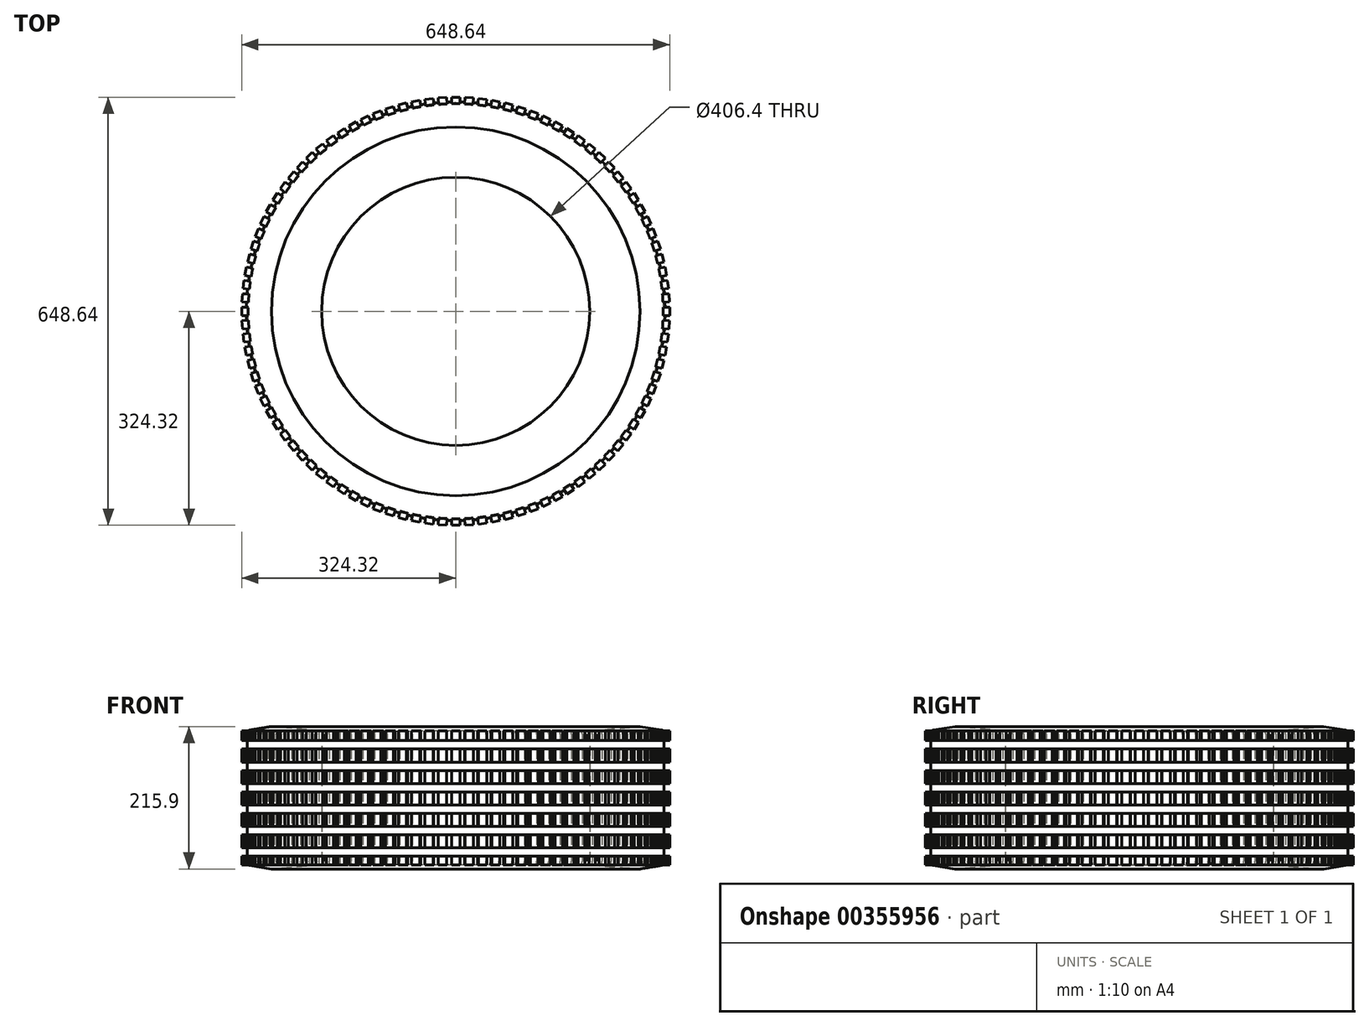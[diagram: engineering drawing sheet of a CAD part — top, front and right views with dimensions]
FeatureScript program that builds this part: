
annotation { "Feature Type Name" : "Feature", "Feature Type Description" : "" }
export const myFeature = defineFeature(function(context is Context, id is Id, definition is map)
    precondition{}
    {
        {
            var Q0;
            Q0=qCreatedBy(makeId("Top.planeOp"),FACE);
            var sketch = newSketch(context, id + "F0", { "sketchPlane" : qUnion([Q0])});
            skCircle(sketch, "E0", {"center": v(0, 0) * mm, "radius": 317.5 * mm});
            skCircle(sketch, "E1", {"center": v(0, 0) * mm, "radius": 203.2 * mm});
            skLineSegment(sketch, "E2", {"start": v(0, 0) * mm, "end": v(0, 317.5) * mm});
            skSolve(sketch);
        }
        {
            var Q0;
            Q0=qSketchRegion(id+"F0",true);
            extrude(context, id + "F1", {"entities" : qUnion([Q0]), "depth" : 209.55 * mm, "hasSecondDirection" : true, "secondDirectionOppositeDirection" : true, "secondDirectionDepth" : 6.35 * mm});
        }
        {
            var Q0;
            Q0=makeQuery(id+"F1.opExtrude","CAP_EDGE",EDGE,{"disambiguationData":[OSD([sQuery(id+"F0.wireOp",EDGE,"E0")])],"isStart":true});
            chamfer(context, id + "F2", {"entities" : qUnion([Q0]), "chamferType" : ChamferType.TWO_OFFSETS, "width1" : 6.35 * mm, "oppositeDirection" : false, "width2" : 38.1 * mm, "tangentPropagation" : true});
        }
        {
            var Q0;
            Q0=makeQuery(id+"F1.opExtrude","CAP_EDGE",EDGE,{"disambiguationData":[OSD([sQuery(id+"F0.wireOp",EDGE,"E0")])],"isStart":false});
            chamfer(context, id + "F3", {"entities" : qUnion([Q0]), "chamferType" : ChamferType.TWO_OFFSETS, "width1" : 6.35 * mm, "oppositeDirection" : true, "width2" : 38.1 * mm, "tangentPropagation" : true});
        }
        {
            var Q0;
            Q0=makeQuery(id+"F1.opExtrude","CAP_EDGE",EDGE,{"disambiguationData":[OSD([sQuery(id+"F0.wireOp",EDGE,"E1")])],"isStart":true});
            chamfer(context, id + "F4", {"entities" : qUnion([Q0]), "chamferType" : ChamferType.TWO_OFFSETS, "width1" : 76.2 * mm, "oppositeDirection" : false, "width2" : 6.35 * mm, "tangentPropagation" : true});
        }
        {
            var Q0;
            Q0=makeQuery(id+"F1.opExtrude","CAP_EDGE",EDGE,{"disambiguationData":[OSD([sQuery(id+"F0.wireOp",EDGE,"E1")])],"isStart":false});
            chamfer(context, id + "F5", {"entities" : qUnion([Q0]), "chamferType" : ChamferType.TWO_OFFSETS, "width1" : 6.35 * mm, "oppositeDirection" : false, "width2" : 76.2 * mm, "tangentPropagation" : true});
        }
        {
            var Q0;
            {var subQ0=sQuery(id+"F0.wireOp",EDGE,"E0");Q0=makeQuery(id+"F2.opChamfer","BLEND_EDGE",EDGE,{"blendedFrom":[makeQuery(id+"F1.opExtrude","CAP_EDGE",EDGE,{"disambiguationData":[OSD([subQ0])],"isStart":true}),makeQuery(id+"F1.opExtrude","SWEPT_FACE",FACE,{"disambiguationData":[OSD([subQ0])]})],"blendedInto":[makeQuery(id+"F1.opExtrude","SWEPT_FACE",FACE,{"disambiguationData":[OSD([subQ0])]})]});}
            var Q1;
            {var subQ0=sQuery(id+"F0.wireOp",EDGE,"E0");Q1=makeQuery(id+"F3.opChamfer","BLEND_EDGE",EDGE,{"blendedFrom":[makeQuery(id+"F1.opExtrude","CAP_EDGE",EDGE,{"disambiguationData":[OSD([subQ0])],"isStart":false}),makeQuery(id+"F1.opExtrude","SWEPT_FACE",FACE,{"disambiguationData":[OSD([subQ0])]})],"blendedInto":[makeQuery(id+"F1.opExtrude","SWEPT_FACE",FACE,{"disambiguationData":[OSD([subQ0])]})]});}
            fillet(context, id + "F6", {"entities" : qUnion([Q0, Q1]), "radius" : 6.35 * mm, "tangentPropagation" : true, "allowEdgeOverflow" : false});
        }
        {
            var Q0;
            Q0=qCreatedBy(makeId("Top.planeOp"),FACE);
            var sketch = newSketch(context, id + "F7", { "sketchPlane" : qUnion([Q0])});
            skLineSegment(sketch, "E3.bottom", {"start": v(6.35, -311.62) * mm, "end": v(-6.35, -311.62) * mm});
            skLineSegment(sketch, "E3.top", {"start": v(6.35, -324.32) * mm, "end": v(-6.35, -324.32) * mm});
            skLineSegment(sketch, "E3.left", {"start": v(6.35, -311.62) * mm, "end": v(6.35, -324.32) * mm});
            skLineSegment(sketch, "E3.right", {"start": v(-6.35, -311.62) * mm, "end": v(-6.35, -324.32) * mm});
            skPoint(sketch, "E3.middle", {"position": v(0, -317.97) * mm});
            skLineSegment(sketch, "E4.1.0", {"start": v(13.23, -311.4) * mm, "end": v(14.03, -324.08) * mm});
            skLineSegment(sketch, "E4.1.1", {"start": v(25.9, -310.61) * mm, "end": v(26.7, -323.29) * mm});
            skLineSegment(sketch, "E4.1.2", {"start": v(26.7, -323.29) * mm, "end": v(14.03, -324.08) * mm});
            skLineSegment(sketch, "E4.1.3", {"start": v(25.9, -310.61) * mm, "end": v(13.23, -311.4) * mm});
            skLineSegment(sketch, "E4.2.0", {"start": v(32.76, -309.96) * mm, "end": v(34.35, -322.56) * mm});
            skLineSegment(sketch, "E4.2.1", {"start": v(45.36, -308.37) * mm, "end": v(46.95, -320.97) * mm});
            skLineSegment(sketch, "E4.2.2", {"start": v(46.95, -320.97) * mm, "end": v(34.35, -322.56) * mm});
            skLineSegment(sketch, "E4.2.3", {"start": v(45.36, -308.37) * mm, "end": v(32.76, -309.96) * mm});
            skLineSegment(sketch, "E4.3.0", {"start": v(52.15, -307.3) * mm, "end": v(54.53, -319.77) * mm});
            skLineSegment(sketch, "E4.3.1", {"start": v(64.63, -304.91) * mm, "end": v(67, -317.39) * mm});
            skLineSegment(sketch, "E4.3.2", {"start": v(67, -317.39) * mm, "end": v(54.53, -319.77) * mm});
            skLineSegment(sketch, "E4.3.3", {"start": v(64.63, -304.91) * mm, "end": v(52.15, -307.3) * mm});
            skLineSegment(sketch, "E4.4.0", {"start": v(71.35, -303.41) * mm, "end": v(74.5, -315.71) * mm});
            skLineSegment(sketch, "E4.4.1", {"start": v(83.65, -300.25) * mm, "end": v(86.8, -312.56) * mm});
            skLineSegment(sketch, "E4.4.2", {"start": v(86.8, -312.56) * mm, "end": v(74.5, -315.71) * mm});
            skLineSegment(sketch, "E4.4.3", {"start": v(83.65, -300.25) * mm, "end": v(71.35, -303.41) * mm});
            skLineSegment(sketch, "E4.5.0", {"start": v(90.26, -298.33) * mm, "end": v(94.18, -310.41) * mm});
            skLineSegment(sketch, "E4.5.1", {"start": v(102.34, -294.4) * mm, "end": v(106.26, -306.49) * mm});
            skLineSegment(sketch, "E4.5.2", {"start": v(106.26, -306.49) * mm, "end": v(94.18, -310.41) * mm});
            skLineSegment(sketch, "E4.5.3", {"start": v(102.34, -294.4) * mm, "end": v(90.26, -298.33) * mm});
            skLineSegment(sketch, "E4.6.0", {"start": v(108.81, -292.08) * mm, "end": v(113.49, -303.89) * mm});
            skLineSegment(sketch, "E4.6.1", {"start": v(120.62, -287.4) * mm, "end": v(125.3, -299.21) * mm});
            skLineSegment(sketch, "E4.6.2", {"start": v(125.3, -299.21) * mm, "end": v(113.49, -303.89) * mm});
            skLineSegment(sketch, "E4.6.3", {"start": v(120.62, -287.4) * mm, "end": v(108.81, -292.08) * mm});
            skLineSegment(sketch, "E4.7.0", {"start": v(126.94, -284.67) * mm, "end": v(132.34, -296.16) * mm});
            skLineSegment(sketch, "E4.7.1", {"start": v(138.43, -279.26) * mm, "end": v(143.84, -290.75) * mm});
            skLineSegment(sketch, "E4.7.2", {"start": v(143.84, -290.75) * mm, "end": v(132.34, -296.16) * mm});
            skLineSegment(sketch, "E4.7.3", {"start": v(138.43, -279.26) * mm, "end": v(126.94, -284.67) * mm});
            skLineSegment(sketch, "E4.8.0", {"start": v(144.56, -276.14) * mm, "end": v(150.68, -287.27) * mm});
            skLineSegment(sketch, "E4.8.1", {"start": v(155.7, -270.02) * mm, "end": v(161.8, -281.15) * mm});
            skLineSegment(sketch, "E4.8.2", {"start": v(161.8, -281.15) * mm, "end": v(150.68, -287.27) * mm});
            skLineSegment(sketch, "E4.8.3", {"start": v(155.7, -270.02) * mm, "end": v(144.56, -276.14) * mm});
            skLineSegment(sketch, "E4.9.0", {"start": v(161.61, -266.52) * mm, "end": v(168.42, -277.24) * mm});
            skLineSegment(sketch, "E4.9.1", {"start": v(172.34, -259.71) * mm, "end": v(179.14, -270.43) * mm});
            skLineSegment(sketch, "E4.9.2", {"start": v(179.14, -270.43) * mm, "end": v(168.42, -277.24) * mm});
            skLineSegment(sketch, "E4.9.3", {"start": v(172.34, -259.71) * mm, "end": v(161.61, -266.52) * mm});
            skLineSegment(sketch, "E4.10.0", {"start": v(178.03, -255.84) * mm, "end": v(185.5, -266.12) * mm});
            skLineSegment(sketch, "E4.10.1", {"start": v(188.3, -248.38) * mm, "end": v(195.77, -258.65) * mm});
            skLineSegment(sketch, "E4.10.2", {"start": v(195.77, -258.65) * mm, "end": v(185.5, -266.12) * mm});
            skLineSegment(sketch, "E4.10.3", {"start": v(188.3, -248.38) * mm, "end": v(178.03, -255.84) * mm});
            skLineSegment(sketch, "E4.11.0", {"start": v(193.74, -244.16) * mm, "end": v(201.84, -253.94) * mm});
            skLineSegment(sketch, "E4.11.1", {"start": v(203.53, -236.06) * mm, "end": v(211.62, -245.85) * mm});
            skLineSegment(sketch, "E4.11.2", {"start": v(211.62, -245.85) * mm, "end": v(201.84, -253.94) * mm});
            skLineSegment(sketch, "E4.11.3", {"start": v(203.53, -236.06) * mm, "end": v(193.74, -244.16) * mm});
            skLineSegment(sketch, "E4.12.0", {"start": v(208.7, -231.51) * mm, "end": v(217.39, -240.77) * mm});
            skLineSegment(sketch, "E4.12.1", {"start": v(217.95, -222.82) * mm, "end": v(226.64, -232.08) * mm});
            skLineSegment(sketch, "E4.12.2", {"start": v(226.64, -232.08) * mm, "end": v(217.39, -240.77) * mm});
            skLineSegment(sketch, "E4.12.3", {"start": v(217.95, -222.82) * mm, "end": v(208.7, -231.51) * mm});
            skLineSegment(sketch, "E4.13.0", {"start": v(222.82, -217.95) * mm, "end": v(232.08, -226.64) * mm});
            skLineSegment(sketch, "E4.13.1", {"start": v(231.51, -208.7) * mm, "end": v(240.77, -217.39) * mm});
            skLineSegment(sketch, "E4.13.2", {"start": v(240.77, -217.39) * mm, "end": v(232.08, -226.64) * mm});
            skLineSegment(sketch, "E4.13.3", {"start": v(231.51, -208.7) * mm, "end": v(222.82, -217.95) * mm});
            skLineSegment(sketch, "E4.14.0", {"start": v(236.06, -203.53) * mm, "end": v(245.85, -211.62) * mm});
            skLineSegment(sketch, "E4.14.1", {"start": v(244.16, -193.74) * mm, "end": v(253.94, -201.84) * mm});
            skLineSegment(sketch, "E4.14.2", {"start": v(253.94, -201.84) * mm, "end": v(245.85, -211.62) * mm});
            skLineSegment(sketch, "E4.14.3", {"start": v(244.16, -193.74) * mm, "end": v(236.06, -203.53) * mm});
            skLineSegment(sketch, "E4.15.0", {"start": v(248.38, -188.3) * mm, "end": v(258.65, -195.77) * mm});
            skLineSegment(sketch, "E4.15.1", {"start": v(255.84, -178.03) * mm, "end": v(266.12, -185.5) * mm});
            skLineSegment(sketch, "E4.15.2", {"start": v(266.12, -185.5) * mm, "end": v(258.65, -195.77) * mm});
            skLineSegment(sketch, "E4.15.3", {"start": v(255.84, -178.03) * mm, "end": v(248.38, -188.3) * mm});
            skLineSegment(sketch, "E4.16.0", {"start": v(259.71, -172.34) * mm, "end": v(270.43, -179.14) * mm});
            skLineSegment(sketch, "E4.16.1", {"start": v(266.52, -161.61) * mm, "end": v(277.24, -168.42) * mm});
            skLineSegment(sketch, "E4.16.2", {"start": v(277.24, -168.42) * mm, "end": v(270.43, -179.14) * mm});
            skLineSegment(sketch, "E4.16.3", {"start": v(266.52, -161.61) * mm, "end": v(259.71, -172.34) * mm});
            skLineSegment(sketch, "E4.17.0", {"start": v(270.02, -155.7) * mm, "end": v(281.15, -161.8) * mm});
            skLineSegment(sketch, "E4.17.1", {"start": v(276.14, -144.56) * mm, "end": v(287.27, -150.68) * mm});
            skLineSegment(sketch, "E4.17.2", {"start": v(287.27, -150.68) * mm, "end": v(281.15, -161.8) * mm});
            skLineSegment(sketch, "E4.17.3", {"start": v(276.14, -144.56) * mm, "end": v(270.02, -155.7) * mm});
            skLineSegment(sketch, "E4.18.0", {"start": v(279.26, -138.43) * mm, "end": v(290.75, -143.84) * mm});
            skLineSegment(sketch, "E4.18.1", {"start": v(284.67, -126.94) * mm, "end": v(296.16, -132.34) * mm});
            skLineSegment(sketch, "E4.18.2", {"start": v(296.16, -132.34) * mm, "end": v(290.75, -143.84) * mm});
            skLineSegment(sketch, "E4.18.3", {"start": v(284.67, -126.94) * mm, "end": v(279.26, -138.43) * mm});
            skLineSegment(sketch, "E4.19.0", {"start": v(287.4, -120.62) * mm, "end": v(299.21, -125.3) * mm});
            skLineSegment(sketch, "E4.19.1", {"start": v(292.08, -108.81) * mm, "end": v(303.89, -113.49) * mm});
            skLineSegment(sketch, "E4.19.2", {"start": v(303.89, -113.49) * mm, "end": v(299.21, -125.3) * mm});
            skLineSegment(sketch, "E4.19.3", {"start": v(292.08, -108.81) * mm, "end": v(287.4, -120.62) * mm});
            skLineSegment(sketch, "E4.20.0", {"start": v(294.4, -102.34) * mm, "end": v(306.49, -106.26) * mm});
            skLineSegment(sketch, "E4.20.1", {"start": v(298.33, -90.26) * mm, "end": v(310.41, -94.18) * mm});
            skLineSegment(sketch, "E4.20.2", {"start": v(310.41, -94.18) * mm, "end": v(306.49, -106.26) * mm});
            skLineSegment(sketch, "E4.20.3", {"start": v(298.33, -90.26) * mm, "end": v(294.4, -102.34) * mm});
            skLineSegment(sketch, "E4.21.0", {"start": v(300.25, -83.65) * mm, "end": v(312.56, -86.8) * mm});
            skLineSegment(sketch, "E4.21.1", {"start": v(303.41, -71.35) * mm, "end": v(315.71, -74.5) * mm});
            skLineSegment(sketch, "E4.21.2", {"start": v(315.71, -74.5) * mm, "end": v(312.56, -86.8) * mm});
            skLineSegment(sketch, "E4.21.3", {"start": v(303.41, -71.35) * mm, "end": v(300.25, -83.65) * mm});
            skLineSegment(sketch, "E4.22.0", {"start": v(304.91, -64.63) * mm, "end": v(317.39, -67) * mm});
            skLineSegment(sketch, "E4.22.1", {"start": v(307.3, -52.15) * mm, "end": v(319.77, -54.53) * mm});
            skLineSegment(sketch, "E4.22.2", {"start": v(319.77, -54.53) * mm, "end": v(317.39, -67) * mm});
            skLineSegment(sketch, "E4.22.3", {"start": v(307.3, -52.15) * mm, "end": v(304.91, -64.63) * mm});
            skLineSegment(sketch, "E4.23.0", {"start": v(308.37, -45.36) * mm, "end": v(320.97, -46.95) * mm});
            skLineSegment(sketch, "E4.23.1", {"start": v(309.96, -32.76) * mm, "end": v(322.56, -34.35) * mm});
            skLineSegment(sketch, "E4.23.2", {"start": v(322.56, -34.35) * mm, "end": v(320.97, -46.95) * mm});
            skLineSegment(sketch, "E4.23.3", {"start": v(309.96, -32.76) * mm, "end": v(308.37, -45.36) * mm});
            skLineSegment(sketch, "E4.24.0", {"start": v(310.61, -25.9) * mm, "end": v(323.29, -26.7) * mm});
            skLineSegment(sketch, "E4.24.1", {"start": v(311.4, -13.23) * mm, "end": v(324.08, -14.03) * mm});
            skLineSegment(sketch, "E4.24.2", {"start": v(324.08, -14.03) * mm, "end": v(323.29, -26.7) * mm});
            skLineSegment(sketch, "E4.24.3", {"start": v(311.4, -13.23) * mm, "end": v(310.61, -25.9) * mm});
            skLineSegment(sketch, "E4.25.0", {"start": v(311.62, -6.35) * mm, "end": v(324.32, -6.35) * mm});
            skLineSegment(sketch, "E4.25.1", {"start": v(311.62, 6.35) * mm, "end": v(324.32, 6.35) * mm});
            skLineSegment(sketch, "E4.25.2", {"start": v(324.32, 6.35) * mm, "end": v(324.32, -6.35) * mm});
            skLineSegment(sketch, "E4.25.3", {"start": v(311.62, 6.35) * mm, "end": v(311.62, -6.35) * mm});
            skLineSegment(sketch, "E4.26.0", {"start": v(311.4, 13.23) * mm, "end": v(324.08, 14.03) * mm});
            skLineSegment(sketch, "E4.26.1", {"start": v(310.61, 25.9) * mm, "end": v(323.29, 26.7) * mm});
            skLineSegment(sketch, "E4.26.2", {"start": v(323.29, 26.7) * mm, "end": v(324.08, 14.03) * mm});
            skLineSegment(sketch, "E4.26.3", {"start": v(310.61, 25.9) * mm, "end": v(311.4, 13.23) * mm});
            skLineSegment(sketch, "E4.27.0", {"start": v(309.96, 32.76) * mm, "end": v(322.56, 34.35) * mm});
            skLineSegment(sketch, "E4.27.1", {"start": v(308.37, 45.36) * mm, "end": v(320.97, 46.95) * mm});
            skLineSegment(sketch, "E4.27.2", {"start": v(320.97, 46.95) * mm, "end": v(322.56, 34.35) * mm});
            skLineSegment(sketch, "E4.27.3", {"start": v(308.37, 45.36) * mm, "end": v(309.96, 32.76) * mm});
            skLineSegment(sketch, "E4.28.0", {"start": v(307.3, 52.15) * mm, "end": v(319.77, 54.53) * mm});
            skLineSegment(sketch, "E4.28.1", {"start": v(304.91, 64.63) * mm, "end": v(317.39, 67) * mm});
            skLineSegment(sketch, "E4.28.2", {"start": v(317.39, 67) * mm, "end": v(319.77, 54.53) * mm});
            skLineSegment(sketch, "E4.28.3", {"start": v(304.91, 64.63) * mm, "end": v(307.3, 52.15) * mm});
            skLineSegment(sketch, "E4.29.0", {"start": v(303.41, 71.35) * mm, "end": v(315.71, 74.5) * mm});
            skLineSegment(sketch, "E4.29.1", {"start": v(300.25, 83.65) * mm, "end": v(312.56, 86.8) * mm});
            skLineSegment(sketch, "E4.29.2", {"start": v(312.56, 86.8) * mm, "end": v(315.71, 74.5) * mm});
            skLineSegment(sketch, "E4.29.3", {"start": v(300.25, 83.65) * mm, "end": v(303.41, 71.35) * mm});
            skLineSegment(sketch, "E4.30.0", {"start": v(298.33, 90.26) * mm, "end": v(310.41, 94.18) * mm});
            skLineSegment(sketch, "E4.30.1", {"start": v(294.4, 102.34) * mm, "end": v(306.49, 106.26) * mm});
            skLineSegment(sketch, "E4.30.2", {"start": v(306.49, 106.26) * mm, "end": v(310.41, 94.18) * mm});
            skLineSegment(sketch, "E4.30.3", {"start": v(294.4, 102.34) * mm, "end": v(298.33, 90.26) * mm});
            skLineSegment(sketch, "E4.31.0", {"start": v(292.08, 108.81) * mm, "end": v(303.89, 113.49) * mm});
            skLineSegment(sketch, "E4.31.1", {"start": v(287.4, 120.62) * mm, "end": v(299.21, 125.3) * mm});
            skLineSegment(sketch, "E4.31.2", {"start": v(299.21, 125.3) * mm, "end": v(303.89, 113.49) * mm});
            skLineSegment(sketch, "E4.31.3", {"start": v(287.4, 120.62) * mm, "end": v(292.08, 108.81) * mm});
            skLineSegment(sketch, "E4.32.0", {"start": v(284.67, 126.94) * mm, "end": v(296.16, 132.34) * mm});
            skLineSegment(sketch, "E4.32.1", {"start": v(279.26, 138.43) * mm, "end": v(290.75, 143.84) * mm});
            skLineSegment(sketch, "E4.32.2", {"start": v(290.75, 143.84) * mm, "end": v(296.16, 132.34) * mm});
            skLineSegment(sketch, "E4.32.3", {"start": v(279.26, 138.43) * mm, "end": v(284.67, 126.94) * mm});
            skLineSegment(sketch, "E4.33.0", {"start": v(276.14, 144.56) * mm, "end": v(287.27, 150.68) * mm});
            skLineSegment(sketch, "E4.33.1", {"start": v(270.02, 155.7) * mm, "end": v(281.15, 161.8) * mm});
            skLineSegment(sketch, "E4.33.2", {"start": v(281.15, 161.8) * mm, "end": v(287.27, 150.68) * mm});
            skLineSegment(sketch, "E4.33.3", {"start": v(270.02, 155.7) * mm, "end": v(276.14, 144.56) * mm});
            skLineSegment(sketch, "E4.34.0", {"start": v(266.52, 161.61) * mm, "end": v(277.24, 168.42) * mm});
            skLineSegment(sketch, "E4.34.1", {"start": v(259.71, 172.34) * mm, "end": v(270.43, 179.14) * mm});
            skLineSegment(sketch, "E4.34.2", {"start": v(270.43, 179.14) * mm, "end": v(277.24, 168.42) * mm});
            skLineSegment(sketch, "E4.34.3", {"start": v(259.71, 172.34) * mm, "end": v(266.52, 161.61) * mm});
            skLineSegment(sketch, "E4.35.0", {"start": v(255.84, 178.03) * mm, "end": v(266.12, 185.5) * mm});
            skLineSegment(sketch, "E4.35.1", {"start": v(248.38, 188.3) * mm, "end": v(258.65, 195.77) * mm});
            skLineSegment(sketch, "E4.35.2", {"start": v(258.65, 195.77) * mm, "end": v(266.12, 185.5) * mm});
            skLineSegment(sketch, "E4.35.3", {"start": v(248.38, 188.3) * mm, "end": v(255.84, 178.03) * mm});
            skLineSegment(sketch, "E4.36.0", {"start": v(244.16, 193.74) * mm, "end": v(253.94, 201.84) * mm});
            skLineSegment(sketch, "E4.36.1", {"start": v(236.06, 203.53) * mm, "end": v(245.85, 211.62) * mm});
            skLineSegment(sketch, "E4.36.2", {"start": v(245.85, 211.62) * mm, "end": v(253.94, 201.84) * mm});
            skLineSegment(sketch, "E4.36.3", {"start": v(236.06, 203.53) * mm, "end": v(244.16, 193.74) * mm});
            skLineSegment(sketch, "E4.37.0", {"start": v(231.51, 208.7) * mm, "end": v(240.77, 217.39) * mm});
            skLineSegment(sketch, "E4.37.1", {"start": v(222.82, 217.95) * mm, "end": v(232.08, 226.64) * mm});
            skLineSegment(sketch, "E4.37.2", {"start": v(232.08, 226.64) * mm, "end": v(240.77, 217.39) * mm});
            skLineSegment(sketch, "E4.37.3", {"start": v(222.82, 217.95) * mm, "end": v(231.51, 208.7) * mm});
            skLineSegment(sketch, "E4.38.0", {"start": v(217.95, 222.82) * mm, "end": v(226.64, 232.08) * mm});
            skLineSegment(sketch, "E4.38.1", {"start": v(208.7, 231.51) * mm, "end": v(217.39, 240.77) * mm});
            skLineSegment(sketch, "E4.38.2", {"start": v(217.39, 240.77) * mm, "end": v(226.64, 232.08) * mm});
            skLineSegment(sketch, "E4.38.3", {"start": v(208.7, 231.51) * mm, "end": v(217.95, 222.82) * mm});
            skLineSegment(sketch, "E4.39.0", {"start": v(203.53, 236.06) * mm, "end": v(211.62, 245.85) * mm});
            skLineSegment(sketch, "E4.39.1", {"start": v(193.74, 244.16) * mm, "end": v(201.84, 253.94) * mm});
            skLineSegment(sketch, "E4.39.2", {"start": v(201.84, 253.94) * mm, "end": v(211.62, 245.85) * mm});
            skLineSegment(sketch, "E4.39.3", {"start": v(193.74, 244.16) * mm, "end": v(203.53, 236.06) * mm});
            skLineSegment(sketch, "E4.40.0", {"start": v(188.3, 248.38) * mm, "end": v(195.77, 258.65) * mm});
            skLineSegment(sketch, "E4.40.1", {"start": v(178.03, 255.84) * mm, "end": v(185.5, 266.12) * mm});
            skLineSegment(sketch, "E4.40.2", {"start": v(185.5, 266.12) * mm, "end": v(195.77, 258.65) * mm});
            skLineSegment(sketch, "E4.40.3", {"start": v(178.03, 255.84) * mm, "end": v(188.3, 248.38) * mm});
            skLineSegment(sketch, "E4.41.0", {"start": v(172.34, 259.71) * mm, "end": v(179.14, 270.43) * mm});
            skLineSegment(sketch, "E4.41.1", {"start": v(161.61, 266.52) * mm, "end": v(168.42, 277.24) * mm});
            skLineSegment(sketch, "E4.41.2", {"start": v(168.42, 277.24) * mm, "end": v(179.14, 270.43) * mm});
            skLineSegment(sketch, "E4.41.3", {"start": v(161.61, 266.52) * mm, "end": v(172.34, 259.71) * mm});
            skLineSegment(sketch, "E4.42.0", {"start": v(155.7, 270.02) * mm, "end": v(161.8, 281.15) * mm});
            skLineSegment(sketch, "E4.42.1", {"start": v(144.56, 276.14) * mm, "end": v(150.68, 287.27) * mm});
            skLineSegment(sketch, "E4.42.2", {"start": v(150.68, 287.27) * mm, "end": v(161.8, 281.15) * mm});
            skLineSegment(sketch, "E4.42.3", {"start": v(144.56, 276.14) * mm, "end": v(155.7, 270.02) * mm});
            skLineSegment(sketch, "E4.43.0", {"start": v(138.43, 279.26) * mm, "end": v(143.84, 290.75) * mm});
            skLineSegment(sketch, "E4.43.1", {"start": v(126.94, 284.67) * mm, "end": v(132.34, 296.16) * mm});
            skLineSegment(sketch, "E4.43.2", {"start": v(132.34, 296.16) * mm, "end": v(143.84, 290.75) * mm});
            skLineSegment(sketch, "E4.43.3", {"start": v(126.94, 284.67) * mm, "end": v(138.43, 279.26) * mm});
            skLineSegment(sketch, "E4.44.0", {"start": v(120.62, 287.4) * mm, "end": v(125.3, 299.21) * mm});
            skLineSegment(sketch, "E4.44.1", {"start": v(108.81, 292.08) * mm, "end": v(113.49, 303.89) * mm});
            skLineSegment(sketch, "E4.44.2", {"start": v(113.49, 303.89) * mm, "end": v(125.3, 299.21) * mm});
            skLineSegment(sketch, "E4.44.3", {"start": v(108.81, 292.08) * mm, "end": v(120.62, 287.4) * mm});
            skLineSegment(sketch, "E4.45.0", {"start": v(102.34, 294.4) * mm, "end": v(106.26, 306.49) * mm});
            skLineSegment(sketch, "E4.45.1", {"start": v(90.26, 298.33) * mm, "end": v(94.18, 310.41) * mm});
            skLineSegment(sketch, "E4.45.2", {"start": v(94.18, 310.41) * mm, "end": v(106.26, 306.49) * mm});
            skLineSegment(sketch, "E4.45.3", {"start": v(90.26, 298.33) * mm, "end": v(102.34, 294.4) * mm});
            skLineSegment(sketch, "E4.46.0", {"start": v(83.65, 300.25) * mm, "end": v(86.8, 312.56) * mm});
            skLineSegment(sketch, "E4.46.1", {"start": v(71.35, 303.41) * mm, "end": v(74.5, 315.71) * mm});
            skLineSegment(sketch, "E4.46.2", {"start": v(74.5, 315.71) * mm, "end": v(86.8, 312.56) * mm});
            skLineSegment(sketch, "E4.46.3", {"start": v(71.35, 303.41) * mm, "end": v(83.65, 300.25) * mm});
            skLineSegment(sketch, "E4.47.0", {"start": v(64.63, 304.91) * mm, "end": v(67, 317.39) * mm});
            skLineSegment(sketch, "E4.47.1", {"start": v(52.15, 307.3) * mm, "end": v(54.53, 319.77) * mm});
            skLineSegment(sketch, "E4.47.2", {"start": v(54.53, 319.77) * mm, "end": v(67, 317.39) * mm});
            skLineSegment(sketch, "E4.47.3", {"start": v(52.15, 307.3) * mm, "end": v(64.63, 304.91) * mm});
            skLineSegment(sketch, "E4.48.0", {"start": v(45.36, 308.37) * mm, "end": v(46.95, 320.97) * mm});
            skLineSegment(sketch, "E4.48.1", {"start": v(32.76, 309.96) * mm, "end": v(34.35, 322.56) * mm});
            skLineSegment(sketch, "E4.48.2", {"start": v(34.35, 322.56) * mm, "end": v(46.95, 320.97) * mm});
            skLineSegment(sketch, "E4.48.3", {"start": v(32.76, 309.96) * mm, "end": v(45.36, 308.37) * mm});
            skLineSegment(sketch, "E4.49.0", {"start": v(25.9, 310.61) * mm, "end": v(26.7, 323.29) * mm});
            skLineSegment(sketch, "E4.49.1", {"start": v(13.23, 311.4) * mm, "end": v(14.03, 324.08) * mm});
            skLineSegment(sketch, "E4.49.2", {"start": v(14.03, 324.08) * mm, "end": v(26.7, 323.29) * mm});
            skLineSegment(sketch, "E4.49.3", {"start": v(13.23, 311.4) * mm, "end": v(25.9, 310.61) * mm});
            skLineSegment(sketch, "E4.50.0", {"start": v(6.35, 311.62) * mm, "end": v(6.35, 324.32) * mm});
            skLineSegment(sketch, "E4.50.1", {"start": v(-6.35, 311.62) * mm, "end": v(-6.35, 324.32) * mm});
            skLineSegment(sketch, "E4.50.2", {"start": v(-6.35, 324.32) * mm, "end": v(6.35, 324.32) * mm});
            skLineSegment(sketch, "E4.50.3", {"start": v(-6.35, 311.62) * mm, "end": v(6.35, 311.62) * mm});
            skLineSegment(sketch, "E4.51.0", {"start": v(-13.23, 311.4) * mm, "end": v(-14.03, 324.08) * mm});
            skLineSegment(sketch, "E4.51.1", {"start": v(-25.9, 310.61) * mm, "end": v(-26.7, 323.29) * mm});
            skLineSegment(sketch, "E4.51.2", {"start": v(-26.7, 323.29) * mm, "end": v(-14.03, 324.08) * mm});
            skLineSegment(sketch, "E4.51.3", {"start": v(-25.9, 310.61) * mm, "end": v(-13.23, 311.4) * mm});
            skLineSegment(sketch, "E4.52.0", {"start": v(-32.76, 309.96) * mm, "end": v(-34.35, 322.56) * mm});
            skLineSegment(sketch, "E4.52.1", {"start": v(-45.36, 308.37) * mm, "end": v(-46.95, 320.97) * mm});
            skLineSegment(sketch, "E4.52.2", {"start": v(-46.95, 320.97) * mm, "end": v(-34.35, 322.56) * mm});
            skLineSegment(sketch, "E4.52.3", {"start": v(-45.36, 308.37) * mm, "end": v(-32.76, 309.96) * mm});
            skLineSegment(sketch, "E4.53.0", {"start": v(-52.15, 307.3) * mm, "end": v(-54.53, 319.77) * mm});
            skLineSegment(sketch, "E4.53.1", {"start": v(-64.63, 304.91) * mm, "end": v(-67, 317.39) * mm});
            skLineSegment(sketch, "E4.53.2", {"start": v(-67, 317.39) * mm, "end": v(-54.53, 319.77) * mm});
            skLineSegment(sketch, "E4.53.3", {"start": v(-64.63, 304.91) * mm, "end": v(-52.15, 307.3) * mm});
            skLineSegment(sketch, "E4.54.0", {"start": v(-71.35, 303.41) * mm, "end": v(-74.5, 315.71) * mm});
            skLineSegment(sketch, "E4.54.1", {"start": v(-83.65, 300.25) * mm, "end": v(-86.8, 312.56) * mm});
            skLineSegment(sketch, "E4.54.2", {"start": v(-86.8, 312.56) * mm, "end": v(-74.5, 315.71) * mm});
            skLineSegment(sketch, "E4.54.3", {"start": v(-83.65, 300.25) * mm, "end": v(-71.35, 303.41) * mm});
            skLineSegment(sketch, "E4.55.0", {"start": v(-90.26, 298.33) * mm, "end": v(-94.18, 310.41) * mm});
            skLineSegment(sketch, "E4.55.1", {"start": v(-102.34, 294.4) * mm, "end": v(-106.26, 306.49) * mm});
            skLineSegment(sketch, "E4.55.2", {"start": v(-106.26, 306.49) * mm, "end": v(-94.18, 310.41) * mm});
            skLineSegment(sketch, "E4.55.3", {"start": v(-102.34, 294.4) * mm, "end": v(-90.26, 298.33) * mm});
            skLineSegment(sketch, "E4.56.0", {"start": v(-108.81, 292.08) * mm, "end": v(-113.49, 303.89) * mm});
            skLineSegment(sketch, "E4.56.1", {"start": v(-120.62, 287.4) * mm, "end": v(-125.3, 299.21) * mm});
            skLineSegment(sketch, "E4.56.2", {"start": v(-125.3, 299.21) * mm, "end": v(-113.49, 303.89) * mm});
            skLineSegment(sketch, "E4.56.3", {"start": v(-120.62, 287.4) * mm, "end": v(-108.81, 292.08) * mm});
            skLineSegment(sketch, "E4.57.0", {"start": v(-126.94, 284.67) * mm, "end": v(-132.34, 296.16) * mm});
            skLineSegment(sketch, "E4.57.1", {"start": v(-138.43, 279.26) * mm, "end": v(-143.84, 290.75) * mm});
            skLineSegment(sketch, "E4.57.2", {"start": v(-143.84, 290.75) * mm, "end": v(-132.34, 296.16) * mm});
            skLineSegment(sketch, "E4.57.3", {"start": v(-138.43, 279.26) * mm, "end": v(-126.94, 284.67) * mm});
            skLineSegment(sketch, "E4.58.0", {"start": v(-144.56, 276.14) * mm, "end": v(-150.68, 287.27) * mm});
            skLineSegment(sketch, "E4.58.1", {"start": v(-155.7, 270.02) * mm, "end": v(-161.8, 281.15) * mm});
            skLineSegment(sketch, "E4.58.2", {"start": v(-161.8, 281.15) * mm, "end": v(-150.68, 287.27) * mm});
            skLineSegment(sketch, "E4.58.3", {"start": v(-155.7, 270.02) * mm, "end": v(-144.56, 276.14) * mm});
            skLineSegment(sketch, "E4.59.0", {"start": v(-161.61, 266.52) * mm, "end": v(-168.42, 277.24) * mm});
            skLineSegment(sketch, "E4.59.1", {"start": v(-172.34, 259.71) * mm, "end": v(-179.14, 270.43) * mm});
            skLineSegment(sketch, "E4.59.2", {"start": v(-179.14, 270.43) * mm, "end": v(-168.42, 277.24) * mm});
            skLineSegment(sketch, "E4.59.3", {"start": v(-172.34, 259.71) * mm, "end": v(-161.61, 266.52) * mm});
            skLineSegment(sketch, "E4.60.0", {"start": v(-178.03, 255.84) * mm, "end": v(-185.5, 266.12) * mm});
            skLineSegment(sketch, "E4.60.1", {"start": v(-188.3, 248.38) * mm, "end": v(-195.77, 258.65) * mm});
            skLineSegment(sketch, "E4.60.2", {"start": v(-195.77, 258.65) * mm, "end": v(-185.5, 266.12) * mm});
            skLineSegment(sketch, "E4.60.3", {"start": v(-188.3, 248.38) * mm, "end": v(-178.03, 255.84) * mm});
            skLineSegment(sketch, "E4.61.0", {"start": v(-193.74, 244.16) * mm, "end": v(-201.84, 253.94) * mm});
            skLineSegment(sketch, "E4.61.1", {"start": v(-203.53, 236.06) * mm, "end": v(-211.62, 245.85) * mm});
            skLineSegment(sketch, "E4.61.2", {"start": v(-211.62, 245.85) * mm, "end": v(-201.84, 253.94) * mm});
            skLineSegment(sketch, "E4.61.3", {"start": v(-203.53, 236.06) * mm, "end": v(-193.74, 244.16) * mm});
            skLineSegment(sketch, "E4.62.0", {"start": v(-208.7, 231.51) * mm, "end": v(-217.39, 240.77) * mm});
            skLineSegment(sketch, "E4.62.1", {"start": v(-217.95, 222.82) * mm, "end": v(-226.64, 232.08) * mm});
            skLineSegment(sketch, "E4.62.2", {"start": v(-226.64, 232.08) * mm, "end": v(-217.39, 240.77) * mm});
            skLineSegment(sketch, "E4.62.3", {"start": v(-217.95, 222.82) * mm, "end": v(-208.7, 231.51) * mm});
            skLineSegment(sketch, "E4.63.0", {"start": v(-222.82, 217.95) * mm, "end": v(-232.08, 226.64) * mm});
            skLineSegment(sketch, "E4.63.1", {"start": v(-231.51, 208.7) * mm, "end": v(-240.77, 217.39) * mm});
            skLineSegment(sketch, "E4.63.2", {"start": v(-240.77, 217.39) * mm, "end": v(-232.08, 226.64) * mm});
            skLineSegment(sketch, "E4.63.3", {"start": v(-231.51, 208.7) * mm, "end": v(-222.82, 217.95) * mm});
            skLineSegment(sketch, "E4.64.0", {"start": v(-236.06, 203.53) * mm, "end": v(-245.85, 211.62) * mm});
            skLineSegment(sketch, "E4.64.1", {"start": v(-244.16, 193.74) * mm, "end": v(-253.94, 201.84) * mm});
            skLineSegment(sketch, "E4.64.2", {"start": v(-253.94, 201.84) * mm, "end": v(-245.85, 211.62) * mm});
            skLineSegment(sketch, "E4.64.3", {"start": v(-244.16, 193.74) * mm, "end": v(-236.06, 203.53) * mm});
            skLineSegment(sketch, "E4.65.0", {"start": v(-248.38, 188.3) * mm, "end": v(-258.65, 195.77) * mm});
            skLineSegment(sketch, "E4.65.1", {"start": v(-255.84, 178.03) * mm, "end": v(-266.12, 185.5) * mm});
            skLineSegment(sketch, "E4.65.2", {"start": v(-266.12, 185.5) * mm, "end": v(-258.65, 195.77) * mm});
            skLineSegment(sketch, "E4.65.3", {"start": v(-255.84, 178.03) * mm, "end": v(-248.38, 188.3) * mm});
            skLineSegment(sketch, "E4.66.0", {"start": v(-259.71, 172.34) * mm, "end": v(-270.43, 179.14) * mm});
            skLineSegment(sketch, "E4.66.1", {"start": v(-266.52, 161.61) * mm, "end": v(-277.24, 168.42) * mm});
            skLineSegment(sketch, "E4.66.2", {"start": v(-277.24, 168.42) * mm, "end": v(-270.43, 179.14) * mm});
            skLineSegment(sketch, "E4.66.3", {"start": v(-266.52, 161.61) * mm, "end": v(-259.71, 172.34) * mm});
            skLineSegment(sketch, "E4.67.0", {"start": v(-270.02, 155.7) * mm, "end": v(-281.15, 161.8) * mm});
            skLineSegment(sketch, "E4.67.1", {"start": v(-276.14, 144.56) * mm, "end": v(-287.27, 150.68) * mm});
            skLineSegment(sketch, "E4.67.2", {"start": v(-287.27, 150.68) * mm, "end": v(-281.15, 161.8) * mm});
            skLineSegment(sketch, "E4.67.3", {"start": v(-276.14, 144.56) * mm, "end": v(-270.02, 155.7) * mm});
            skLineSegment(sketch, "E4.68.0", {"start": v(-279.26, 138.43) * mm, "end": v(-290.75, 143.84) * mm});
            skLineSegment(sketch, "E4.68.1", {"start": v(-284.67, 126.94) * mm, "end": v(-296.16, 132.34) * mm});
            skLineSegment(sketch, "E4.68.2", {"start": v(-296.16, 132.34) * mm, "end": v(-290.75, 143.84) * mm});
            skLineSegment(sketch, "E4.68.3", {"start": v(-284.67, 126.94) * mm, "end": v(-279.26, 138.43) * mm});
            skLineSegment(sketch, "E4.69.0", {"start": v(-287.4, 120.62) * mm, "end": v(-299.21, 125.3) * mm});
            skLineSegment(sketch, "E4.69.1", {"start": v(-292.08, 108.81) * mm, "end": v(-303.89, 113.49) * mm});
            skLineSegment(sketch, "E4.69.2", {"start": v(-303.89, 113.49) * mm, "end": v(-299.21, 125.3) * mm});
            skLineSegment(sketch, "E4.69.3", {"start": v(-292.08, 108.81) * mm, "end": v(-287.4, 120.62) * mm});
            skLineSegment(sketch, "E4.70.0", {"start": v(-294.4, 102.34) * mm, "end": v(-306.49, 106.26) * mm});
            skLineSegment(sketch, "E4.70.1", {"start": v(-298.33, 90.26) * mm, "end": v(-310.41, 94.18) * mm});
            skLineSegment(sketch, "E4.70.2", {"start": v(-310.41, 94.18) * mm, "end": v(-306.49, 106.26) * mm});
            skLineSegment(sketch, "E4.70.3", {"start": v(-298.33, 90.26) * mm, "end": v(-294.4, 102.34) * mm});
            skLineSegment(sketch, "E4.71.0", {"start": v(-300.25, 83.65) * mm, "end": v(-312.56, 86.8) * mm});
            skLineSegment(sketch, "E4.71.1", {"start": v(-303.41, 71.35) * mm, "end": v(-315.71, 74.5) * mm});
            skLineSegment(sketch, "E4.71.2", {"start": v(-315.71, 74.5) * mm, "end": v(-312.56, 86.8) * mm});
            skLineSegment(sketch, "E4.71.3", {"start": v(-303.41, 71.35) * mm, "end": v(-300.25, 83.65) * mm});
            skLineSegment(sketch, "E4.72.0", {"start": v(-304.91, 64.63) * mm, "end": v(-317.39, 67) * mm});
            skLineSegment(sketch, "E4.72.1", {"start": v(-307.3, 52.15) * mm, "end": v(-319.77, 54.53) * mm});
            skLineSegment(sketch, "E4.72.2", {"start": v(-319.77, 54.53) * mm, "end": v(-317.39, 67) * mm});
            skLineSegment(sketch, "E4.72.3", {"start": v(-307.3, 52.15) * mm, "end": v(-304.91, 64.63) * mm});
            skLineSegment(sketch, "E4.73.0", {"start": v(-308.37, 45.36) * mm, "end": v(-320.97, 46.95) * mm});
            skLineSegment(sketch, "E4.73.1", {"start": v(-309.96, 32.76) * mm, "end": v(-322.56, 34.35) * mm});
            skLineSegment(sketch, "E4.73.2", {"start": v(-322.56, 34.35) * mm, "end": v(-320.97, 46.95) * mm});
            skLineSegment(sketch, "E4.73.3", {"start": v(-309.96, 32.76) * mm, "end": v(-308.37, 45.36) * mm});
            skLineSegment(sketch, "E4.74.0", {"start": v(-310.61, 25.9) * mm, "end": v(-323.29, 26.7) * mm});
            skLineSegment(sketch, "E4.74.1", {"start": v(-311.4, 13.23) * mm, "end": v(-324.08, 14.03) * mm});
            skLineSegment(sketch, "E4.74.2", {"start": v(-324.08, 14.03) * mm, "end": v(-323.29, 26.7) * mm});
            skLineSegment(sketch, "E4.74.3", {"start": v(-311.4, 13.23) * mm, "end": v(-310.61, 25.9) * mm});
            skLineSegment(sketch, "E4.75.0", {"start": v(-311.62, 6.35) * mm, "end": v(-324.32, 6.35) * mm});
            skLineSegment(sketch, "E4.75.1", {"start": v(-311.62, -6.35) * mm, "end": v(-324.32, -6.35) * mm});
            skLineSegment(sketch, "E4.75.2", {"start": v(-324.32, -6.35) * mm, "end": v(-324.32, 6.35) * mm});
            skLineSegment(sketch, "E4.75.3", {"start": v(-311.62, -6.35) * mm, "end": v(-311.62, 6.35) * mm});
            skLineSegment(sketch, "E4.76.0", {"start": v(-311.4, -13.23) * mm, "end": v(-324.08, -14.03) * mm});
            skLineSegment(sketch, "E4.76.1", {"start": v(-310.61, -25.9) * mm, "end": v(-323.29, -26.7) * mm});
            skLineSegment(sketch, "E4.76.2", {"start": v(-323.29, -26.7) * mm, "end": v(-324.08, -14.03) * mm});
            skLineSegment(sketch, "E4.76.3", {"start": v(-310.61, -25.9) * mm, "end": v(-311.4, -13.23) * mm});
            skLineSegment(sketch, "E4.77.0", {"start": v(-309.96, -32.76) * mm, "end": v(-322.56, -34.35) * mm});
            skLineSegment(sketch, "E4.77.1", {"start": v(-308.37, -45.36) * mm, "end": v(-320.97, -46.95) * mm});
            skLineSegment(sketch, "E4.77.2", {"start": v(-320.97, -46.95) * mm, "end": v(-322.56, -34.35) * mm});
            skLineSegment(sketch, "E4.77.3", {"start": v(-308.37, -45.36) * mm, "end": v(-309.96, -32.76) * mm});
            skLineSegment(sketch, "E4.78.0", {"start": v(-307.3, -52.15) * mm, "end": v(-319.77, -54.53) * mm});
            skLineSegment(sketch, "E4.78.1", {"start": v(-304.91, -64.63) * mm, "end": v(-317.39, -67) * mm});
            skLineSegment(sketch, "E4.78.2", {"start": v(-317.39, -67) * mm, "end": v(-319.77, -54.53) * mm});
            skLineSegment(sketch, "E4.78.3", {"start": v(-304.91, -64.63) * mm, "end": v(-307.3, -52.15) * mm});
            skLineSegment(sketch, "E4.79.0", {"start": v(-303.41, -71.35) * mm, "end": v(-315.71, -74.5) * mm});
            skLineSegment(sketch, "E4.79.1", {"start": v(-300.25, -83.65) * mm, "end": v(-312.56, -86.8) * mm});
            skLineSegment(sketch, "E4.79.2", {"start": v(-312.56, -86.8) * mm, "end": v(-315.71, -74.5) * mm});
            skLineSegment(sketch, "E4.79.3", {"start": v(-300.25, -83.65) * mm, "end": v(-303.41, -71.35) * mm});
            skLineSegment(sketch, "E4.80.0", {"start": v(-298.33, -90.26) * mm, "end": v(-310.41, -94.18) * mm});
            skLineSegment(sketch, "E4.80.1", {"start": v(-294.4, -102.34) * mm, "end": v(-306.49, -106.26) * mm});
            skLineSegment(sketch, "E4.80.2", {"start": v(-306.49, -106.26) * mm, "end": v(-310.41, -94.18) * mm});
            skLineSegment(sketch, "E4.80.3", {"start": v(-294.4, -102.34) * mm, "end": v(-298.33, -90.26) * mm});
            skLineSegment(sketch, "E4.81.0", {"start": v(-292.08, -108.81) * mm, "end": v(-303.89, -113.49) * mm});
            skLineSegment(sketch, "E4.81.1", {"start": v(-287.4, -120.62) * mm, "end": v(-299.21, -125.3) * mm});
            skLineSegment(sketch, "E4.81.2", {"start": v(-299.21, -125.3) * mm, "end": v(-303.89, -113.49) * mm});
            skLineSegment(sketch, "E4.81.3", {"start": v(-287.4, -120.62) * mm, "end": v(-292.08, -108.81) * mm});
            skLineSegment(sketch, "E4.82.0", {"start": v(-284.67, -126.94) * mm, "end": v(-296.16, -132.34) * mm});
            skLineSegment(sketch, "E4.82.1", {"start": v(-279.26, -138.43) * mm, "end": v(-290.75, -143.84) * mm});
            skLineSegment(sketch, "E4.82.2", {"start": v(-290.75, -143.84) * mm, "end": v(-296.16, -132.34) * mm});
            skLineSegment(sketch, "E4.82.3", {"start": v(-279.26, -138.43) * mm, "end": v(-284.67, -126.94) * mm});
            skLineSegment(sketch, "E4.83.0", {"start": v(-276.14, -144.56) * mm, "end": v(-287.27, -150.68) * mm});
            skLineSegment(sketch, "E4.83.1", {"start": v(-270.02, -155.7) * mm, "end": v(-281.15, -161.8) * mm});
            skLineSegment(sketch, "E4.83.2", {"start": v(-281.15, -161.8) * mm, "end": v(-287.27, -150.68) * mm});
            skLineSegment(sketch, "E4.83.3", {"start": v(-270.02, -155.7) * mm, "end": v(-276.14, -144.56) * mm});
            skLineSegment(sketch, "E4.84.0", {"start": v(-266.52, -161.61) * mm, "end": v(-277.24, -168.42) * mm});
            skLineSegment(sketch, "E4.84.1", {"start": v(-259.71, -172.34) * mm, "end": v(-270.43, -179.14) * mm});
            skLineSegment(sketch, "E4.84.2", {"start": v(-270.43, -179.14) * mm, "end": v(-277.24, -168.42) * mm});
            skLineSegment(sketch, "E4.84.3", {"start": v(-259.71, -172.34) * mm, "end": v(-266.52, -161.61) * mm});
            skLineSegment(sketch, "E4.85.0", {"start": v(-255.84, -178.03) * mm, "end": v(-266.12, -185.5) * mm});
            skLineSegment(sketch, "E4.85.1", {"start": v(-248.38, -188.3) * mm, "end": v(-258.65, -195.77) * mm});
            skLineSegment(sketch, "E4.85.2", {"start": v(-258.65, -195.77) * mm, "end": v(-266.12, -185.5) * mm});
            skLineSegment(sketch, "E4.85.3", {"start": v(-248.38, -188.3) * mm, "end": v(-255.84, -178.03) * mm});
            skLineSegment(sketch, "E4.86.0", {"start": v(-244.16, -193.74) * mm, "end": v(-253.94, -201.84) * mm});
            skLineSegment(sketch, "E4.86.1", {"start": v(-236.06, -203.53) * mm, "end": v(-245.85, -211.62) * mm});
            skLineSegment(sketch, "E4.86.2", {"start": v(-245.85, -211.62) * mm, "end": v(-253.94, -201.84) * mm});
            skLineSegment(sketch, "E4.86.3", {"start": v(-236.06, -203.53) * mm, "end": v(-244.16, -193.74) * mm});
            skLineSegment(sketch, "E4.87.0", {"start": v(-231.51, -208.7) * mm, "end": v(-240.77, -217.39) * mm});
            skLineSegment(sketch, "E4.87.1", {"start": v(-222.82, -217.95) * mm, "end": v(-232.08, -226.64) * mm});
            skLineSegment(sketch, "E4.87.2", {"start": v(-232.08, -226.64) * mm, "end": v(-240.77, -217.39) * mm});
            skLineSegment(sketch, "E4.87.3", {"start": v(-222.82, -217.95) * mm, "end": v(-231.51, -208.7) * mm});
            skLineSegment(sketch, "E4.88.0", {"start": v(-217.95, -222.82) * mm, "end": v(-226.64, -232.08) * mm});
            skLineSegment(sketch, "E4.88.1", {"start": v(-208.7, -231.51) * mm, "end": v(-217.39, -240.77) * mm});
            skLineSegment(sketch, "E4.88.2", {"start": v(-217.39, -240.77) * mm, "end": v(-226.64, -232.08) * mm});
            skLineSegment(sketch, "E4.88.3", {"start": v(-208.7, -231.51) * mm, "end": v(-217.95, -222.82) * mm});
            skLineSegment(sketch, "E4.89.0", {"start": v(-203.53, -236.06) * mm, "end": v(-211.62, -245.85) * mm});
            skLineSegment(sketch, "E4.89.1", {"start": v(-193.74, -244.16) * mm, "end": v(-201.84, -253.94) * mm});
            skLineSegment(sketch, "E4.89.2", {"start": v(-201.84, -253.94) * mm, "end": v(-211.62, -245.85) * mm});
            skLineSegment(sketch, "E4.89.3", {"start": v(-193.74, -244.16) * mm, "end": v(-203.53, -236.06) * mm});
            skLineSegment(sketch, "E4.90.0", {"start": v(-188.3, -248.38) * mm, "end": v(-195.77, -258.65) * mm});
            skLineSegment(sketch, "E4.90.1", {"start": v(-178.03, -255.84) * mm, "end": v(-185.5, -266.12) * mm});
            skLineSegment(sketch, "E4.90.2", {"start": v(-185.5, -266.12) * mm, "end": v(-195.77, -258.65) * mm});
            skLineSegment(sketch, "E4.90.3", {"start": v(-178.03, -255.84) * mm, "end": v(-188.3, -248.38) * mm});
            skLineSegment(sketch, "E4.91.0", {"start": v(-172.34, -259.71) * mm, "end": v(-179.14, -270.43) * mm});
            skLineSegment(sketch, "E4.91.1", {"start": v(-161.61, -266.52) * mm, "end": v(-168.42, -277.24) * mm});
            skLineSegment(sketch, "E4.91.2", {"start": v(-168.42, -277.24) * mm, "end": v(-179.14, -270.43) * mm});
            skLineSegment(sketch, "E4.91.3", {"start": v(-161.61, -266.52) * mm, "end": v(-172.34, -259.71) * mm});
            skLineSegment(sketch, "E4.92.0", {"start": v(-155.7, -270.02) * mm, "end": v(-161.8, -281.15) * mm});
            skLineSegment(sketch, "E4.92.1", {"start": v(-144.56, -276.14) * mm, "end": v(-150.68, -287.27) * mm});
            skLineSegment(sketch, "E4.92.2", {"start": v(-150.68, -287.27) * mm, "end": v(-161.8, -281.15) * mm});
            skLineSegment(sketch, "E4.92.3", {"start": v(-144.56, -276.14) * mm, "end": v(-155.7, -270.02) * mm});
            skLineSegment(sketch, "E4.93.0", {"start": v(-138.43, -279.26) * mm, "end": v(-143.84, -290.75) * mm});
            skLineSegment(sketch, "E4.93.1", {"start": v(-126.94, -284.67) * mm, "end": v(-132.34, -296.16) * mm});
            skLineSegment(sketch, "E4.93.2", {"start": v(-132.34, -296.16) * mm, "end": v(-143.84, -290.75) * mm});
            skLineSegment(sketch, "E4.93.3", {"start": v(-126.94, -284.67) * mm, "end": v(-138.43, -279.26) * mm});
            skLineSegment(sketch, "E4.94.0", {"start": v(-120.62, -287.4) * mm, "end": v(-125.3, -299.21) * mm});
            skLineSegment(sketch, "E4.94.1", {"start": v(-108.81, -292.08) * mm, "end": v(-113.49, -303.89) * mm});
            skLineSegment(sketch, "E4.94.2", {"start": v(-113.49, -303.89) * mm, "end": v(-125.3, -299.21) * mm});
            skLineSegment(sketch, "E4.94.3", {"start": v(-108.81, -292.08) * mm, "end": v(-120.62, -287.4) * mm});
            skLineSegment(sketch, "E4.95.0", {"start": v(-102.34, -294.4) * mm, "end": v(-106.26, -306.49) * mm});
            skLineSegment(sketch, "E4.95.1", {"start": v(-90.26, -298.33) * mm, "end": v(-94.18, -310.41) * mm});
            skLineSegment(sketch, "E4.95.2", {"start": v(-94.18, -310.41) * mm, "end": v(-106.26, -306.49) * mm});
            skLineSegment(sketch, "E4.95.3", {"start": v(-90.26, -298.33) * mm, "end": v(-102.34, -294.4) * mm});
            skLineSegment(sketch, "E4.96.0", {"start": v(-83.65, -300.25) * mm, "end": v(-86.8, -312.56) * mm});
            skLineSegment(sketch, "E4.96.1", {"start": v(-71.35, -303.41) * mm, "end": v(-74.5, -315.71) * mm});
            skLineSegment(sketch, "E4.96.2", {"start": v(-74.5, -315.71) * mm, "end": v(-86.8, -312.56) * mm});
            skLineSegment(sketch, "E4.96.3", {"start": v(-71.35, -303.41) * mm, "end": v(-83.65, -300.25) * mm});
            skLineSegment(sketch, "E4.97.0", {"start": v(-64.63, -304.91) * mm, "end": v(-67, -317.39) * mm});
            skLineSegment(sketch, "E4.97.1", {"start": v(-52.15, -307.3) * mm, "end": v(-54.53, -319.77) * mm});
            skLineSegment(sketch, "E4.97.2", {"start": v(-54.53, -319.77) * mm, "end": v(-67, -317.39) * mm});
            skLineSegment(sketch, "E4.97.3", {"start": v(-52.15, -307.3) * mm, "end": v(-64.63, -304.91) * mm});
            skLineSegment(sketch, "E4.98.0", {"start": v(-45.36, -308.37) * mm, "end": v(-46.95, -320.97) * mm});
            skLineSegment(sketch, "E4.98.1", {"start": v(-32.76, -309.96) * mm, "end": v(-34.35, -322.56) * mm});
            skLineSegment(sketch, "E4.98.2", {"start": v(-34.35, -322.56) * mm, "end": v(-46.95, -320.97) * mm});
            skLineSegment(sketch, "E4.98.3", {"start": v(-32.76, -309.96) * mm, "end": v(-45.36, -308.37) * mm});
            skLineSegment(sketch, "E4.99.0", {"start": v(-25.9, -310.61) * mm, "end": v(-26.7, -323.29) * mm});
            skLineSegment(sketch, "E4.99.1", {"start": v(-13.23, -311.4) * mm, "end": v(-14.03, -324.08) * mm});
            skLineSegment(sketch, "E4.99.2", {"start": v(-14.03, -324.08) * mm, "end": v(-26.7, -323.29) * mm});
            skLineSegment(sketch, "E4.99.3", {"start": v(-13.23, -311.4) * mm, "end": v(-25.9, -310.61) * mm});
            skPoint(sketch, "E4.center", {"position": v(0, 0) * mm});
            skSolve(sketch);
        }
        {
            var Q0;
            Q0=qSketchRegion(id+"F7",true);
            extrude(context, id + "F8", {"entities" : qUnion([Q0]), "operationType" : NewBodyOperationType.ADD, "depth" : 203.2 * mm});
        }
        {
            var Q0;
            Q0=qCreatedBy(makeId("Right.planeOp"),FACE);
            var sketch = newSketch(context, id + "F9", { "sketchPlane" : qUnion([Q0])});
            skLineSegment(sketch, "E5.bottom", {"start": v(316.02, 12.83) * mm, "end": v(328.72, 12.83) * mm});
            skLineSegment(sketch, "E5.top", {"start": v(316.02, 25.53) * mm, "end": v(328.72, 25.53) * mm});
            skLineSegment(sketch, "E5.left", {"start": v(316.02, 12.83) * mm, "end": v(316.02, 25.53) * mm});
            skLineSegment(sketch, "E5.right", {"start": v(328.72, 12.83) * mm, "end": v(328.72, 25.53) * mm});
            skPoint(sketch, "E5.middle", {"position": v(322.37, 19.18) * mm});
            skLineSegment(sketch, "E6.0.1.0", {"start": v(316.02, 45.34) * mm, "end": v(328.72, 45.34) * mm});
            skLineSegment(sketch, "E6.0.1.1", {"start": v(328.72, 45.34) * mm, "end": v(328.72, 58.04) * mm});
            skLineSegment(sketch, "E6.0.1.2", {"start": v(316.02, 58.04) * mm, "end": v(328.72, 58.04) * mm});
            skLineSegment(sketch, "E6.0.1.3", {"start": v(316.02, 45.34) * mm, "end": v(316.02, 58.04) * mm});
            skLineSegment(sketch, "E6.0.2.0", {"start": v(316.02, 77.86) * mm, "end": v(328.72, 77.86) * mm});
            skLineSegment(sketch, "E6.0.2.1", {"start": v(328.72, 77.86) * mm, "end": v(328.72, 90.56) * mm});
            skLineSegment(sketch, "E6.0.2.2", {"start": v(316.02, 90.56) * mm, "end": v(328.72, 90.56) * mm});
            skLineSegment(sketch, "E6.0.2.3", {"start": v(316.02, 77.86) * mm, "end": v(316.02, 90.56) * mm});
            skLineSegment(sketch, "E6.0.3.0", {"start": v(316.02, 110.37) * mm, "end": v(328.72, 110.37) * mm});
            skLineSegment(sketch, "E6.0.3.1", {"start": v(328.72, 110.37) * mm, "end": v(328.72, 123.07) * mm});
            skLineSegment(sketch, "E6.0.3.2", {"start": v(316.02, 123.07) * mm, "end": v(328.72, 123.07) * mm});
            skLineSegment(sketch, "E6.0.3.3", {"start": v(316.02, 110.37) * mm, "end": v(316.02, 123.07) * mm});
            skLineSegment(sketch, "E6.0.4.0", {"start": v(316.02, 142.88) * mm, "end": v(328.72, 142.88) * mm});
            skLineSegment(sketch, "E6.0.4.1", {"start": v(328.72, 142.88) * mm, "end": v(328.72, 155.58) * mm});
            skLineSegment(sketch, "E6.0.4.2", {"start": v(316.02, 155.58) * mm, "end": v(328.72, 155.58) * mm});
            skLineSegment(sketch, "E6.0.4.3", {"start": v(316.02, 142.88) * mm, "end": v(316.02, 155.58) * mm});
            skLineSegment(sketch, "E6.0.5.0", {"start": v(316.02, 175.4) * mm, "end": v(328.72, 175.4) * mm});
            skLineSegment(sketch, "E6.0.5.1", {"start": v(328.72, 175.4) * mm, "end": v(328.72, 188.1) * mm});
            skLineSegment(sketch, "E6.0.5.2", {"start": v(316.02, 188.1) * mm, "end": v(328.72, 188.1) * mm});
            skLineSegment(sketch, "E6.0.5.3", {"start": v(316.02, 175.4) * mm, "end": v(316.02, 188.1) * mm});
            skLineSegment(sketch, "E6.direction1", {"start": v(316.02, 12.83) * mm, "end": v(341.42, 12.83) * mm, "construction": true});
            skLineSegment(sketch, "E6.direction2", {"start": v(316.02, 12.83) * mm, "end": v(316.02, 45.34) * mm, "construction": true});
            skSolve(sketch);
        }
        {
            var Q0;
            Q0=makeQuery(id+"F9.imprint","IMPRINT",FACE,{"disambiguationData":[TD([[makeQuery(id+"F9.imprint","IMPRINT",EDGE,{"derivedFrom":sQuery(id+"F9.wireOp",EDGE,"E6.0.5.0")}),1.0]])]});
            var Q1;
            Q1=makeQuery(id+"F9.imprint","IMPRINT",FACE,{"disambiguationData":[TD([[makeQuery(id+"F9.imprint","IMPRINT",EDGE,{"derivedFrom":sQuery(id+"F9.wireOp",EDGE,"E6.0.4.0")}),1.0]])]});
            var Q2;
            Q2=makeQuery(id+"F9.imprint","IMPRINT",FACE,{"disambiguationData":[TD([[makeQuery(id+"F9.imprint","IMPRINT",EDGE,{"derivedFrom":sQuery(id+"F9.wireOp",EDGE,"E6.0.3.0")}),1.0]])]});
            var Q3;
            Q3=makeQuery(id+"F9.imprint","IMPRINT",FACE,{"disambiguationData":[TD([[makeQuery(id+"F9.imprint","IMPRINT",EDGE,{"derivedFrom":sQuery(id+"F9.wireOp",EDGE,"E6.0.2.0")}),1.0]])]});
            var Q4;
            Q4=makeQuery(id+"F9.imprint","IMPRINT",FACE,{"disambiguationData":[TD([[makeQuery(id+"F9.imprint","IMPRINT",EDGE,{"derivedFrom":sQuery(id+"F9.wireOp",EDGE,"E6.0.1.0")}),1.0]])]});
            var Q5;
            Q5=makeQuery(id+"F9.imprint","IMPRINT",FACE,{"disambiguationData":[TD([[makeQuery(id+"F9.imprint","IMPRINT",EDGE,{"derivedFrom":sQuery(id+"F9.wireOp",EDGE,"E5.bottom")}),1.0]])]});
            var Q6;
            {var subQ0=sQuery(id+"F0.wireOp",EDGE,"E0");Q6=makeQuery(id+"F6.opFillet","BLEND_EDGE",EDGE,{"blendedFrom":[makeQuery(id+"F2.opChamfer","BLEND_EDGE",EDGE,{"blendedFrom":[makeQuery(id+"F1.opExtrude","CAP_EDGE",EDGE,{"disambiguationData":[OSD([subQ0])],"isStart":true}),makeQuery(id+"F1.opExtrude","SWEPT_FACE",FACE,{"disambiguationData":[OSD([subQ0])]})],"blendedInto":[makeQuery(id+"F1.opExtrude","SWEPT_FACE",FACE,{"disambiguationData":[OSD([subQ0])]})]}),makeQuery(id+"F2.opChamfer","BLEND_FACE",FACE,{"disambiguationData":[OSD([subQ0])]})],"blendedInto":[makeQuery(id+"F2.opChamfer","BLEND_FACE",FACE,{"disambiguationData":[OSD([subQ0])]})]});}
            revolve(context, id + "F10", {"operationType" : NewBodyOperationType.REMOVE, "entities" : qUnion([Q0, Q1, Q2, Q3, Q4, Q5]), "axis" : qUnion([Q6]), "revolveType" : RevolveType.FULL, "oppositeDirection" : true});
        }
    });
